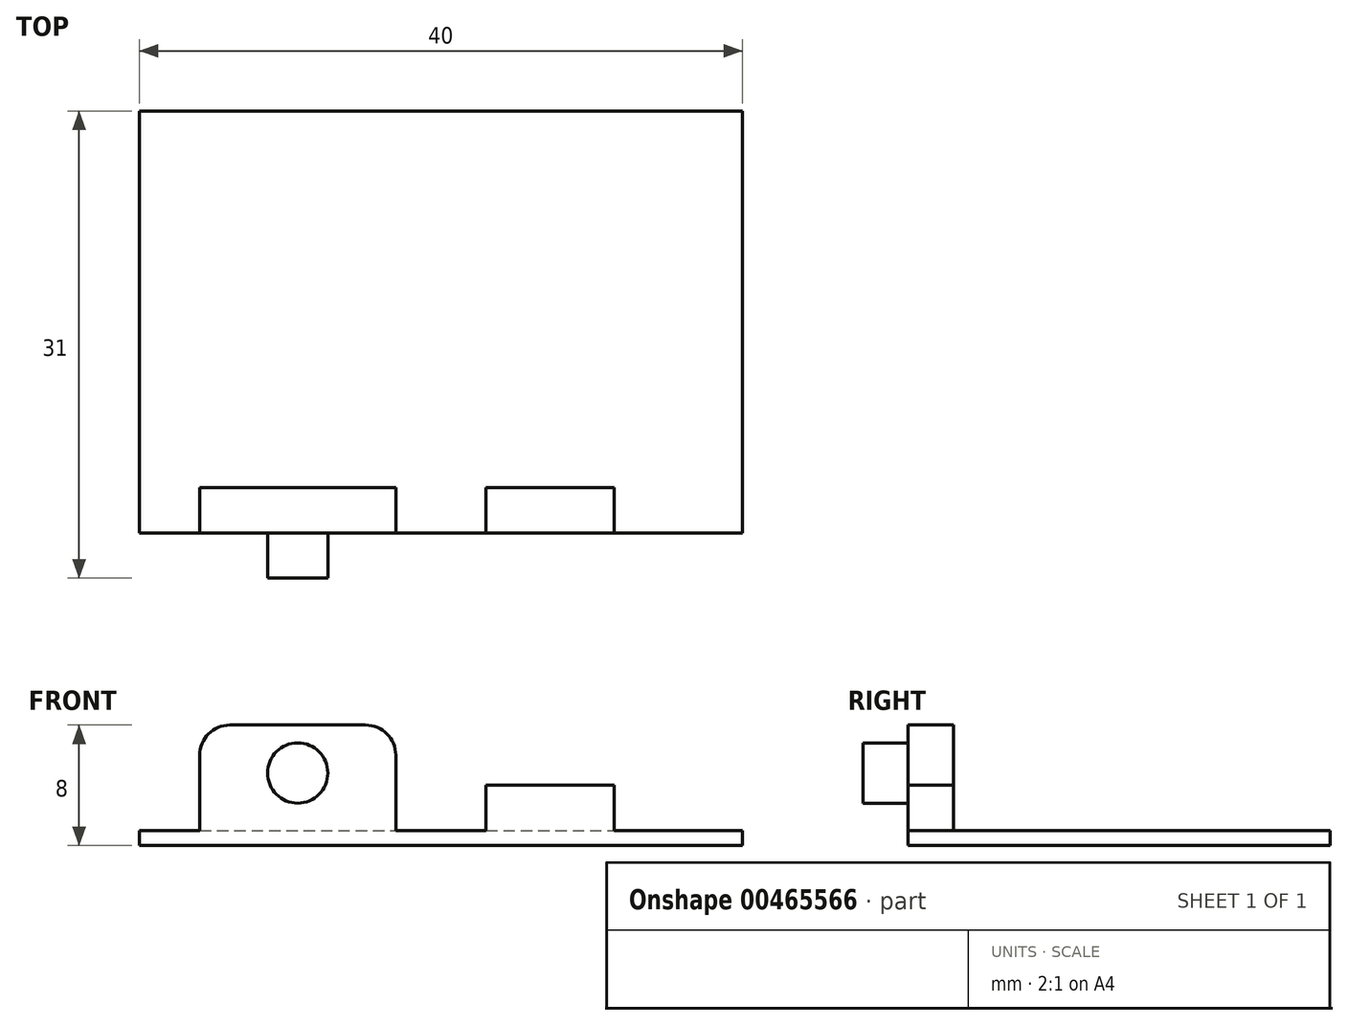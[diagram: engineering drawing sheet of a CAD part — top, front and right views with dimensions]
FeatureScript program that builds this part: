
annotation { "Feature Type Name" : "Feature", "Feature Type Description" : "" }
export const myFeature = defineFeature(function(context is Context, id is Id, definition is map)
    precondition{}
    {
        {
            var Q0;
            Q0=qCreatedBy(makeId("Top.planeOp"),FACE);
            var sketch = newSketch(context, id + "F0", { "sketchPlane" : qUnion([Q0])});
            skLineSegment(sketch, "E0.bottom", {"start": v(20, 14) * mm, "end": v(-20, 14) * mm});
            skLineSegment(sketch, "E0.top", {"start": v(20, -14) * mm, "end": v(-20, -14) * mm});
            skLineSegment(sketch, "E0.left", {"start": v(20, 14) * mm, "end": v(20, -14) * mm});
            skLineSegment(sketch, "E0.right", {"start": v(-20, 14) * mm, "end": v(-20, -14) * mm});
            skPoint(sketch, "E0.middle", {"position": v(0, 0) * mm});
            skSolve(sketch);
        }
        {
            var Q0;
            Q0=makeQuery(id+"F0.imprint","IMPRINT",FACE,{"disambiguationData":[TD([[makeQuery(id+"F0.imprint","IMPRINT",EDGE,{"derivedFrom":sQuery(id+"F0.wireOp",EDGE,"E0.bottom")}),1.0]])]});
            extrude(context, id + "F1", {"entities" : qUnion([Q0]), "depth" : 1 * mm});
        }
        {
            var Q0;
            Q0=makeQuery(id+"F1.opExtrude","CAP_FACE",FACE,{"disambiguationData":[OSD([sQuery(id+"F0.wireOp",EDGE,"E0.bottom"),sQuery(id+"F0.wireOp",EDGE,"E0.top"),sQuery(id+"F0.wireOp",EDGE,"E0.left"),sQuery(id+"F0.wireOp",EDGE,"E0.right")])],"isStart":false});
            var sketch = newSketch(context, id + "F2", { "sketchPlane" : qUnion([Q0])});
            skLineSegment(sketch, "E1.bottom", {"start": v(3, -14) * mm, "end": v(11.5, -14) * mm});
            skLineSegment(sketch, "E1.top", {"start": v(3, -11) * mm, "end": v(11.5, -11) * mm});
            skLineSegment(sketch, "E1.left", {"start": v(3, -14) * mm, "end": v(3, -11) * mm});
            skLineSegment(sketch, "E1.right", {"start": v(11.5, -14) * mm, "end": v(11.5, -11) * mm});
            skLineSegment(sketch, "E2.bottom", {"start": v(-16, -14) * mm, "end": v(-3, -14) * mm});
            skLineSegment(sketch, "E2.top", {"start": v(-16, -11) * mm, "end": v(-3, -11) * mm});
            skLineSegment(sketch, "E2.left", {"start": v(-16, -14) * mm, "end": v(-16, -11) * mm});
            skLineSegment(sketch, "E2.right", {"start": v(-3, -14) * mm, "end": v(-3, -11) * mm});
            skSolve(sketch);
        }
        {
            var Q0;
            Q0=makeQuery(id+"F2.imprint","IMPRINT",FACE,{"disambiguationData":[TD([[makeQuery(id+"F2.imprint","IMPRINT",EDGE,{"derivedFrom":sQuery(id+"F2.wireOp",EDGE,"E2.bottom")}),-1.0]])]});
            extrude(context, id + "F3", {"entities" : qUnion([Q0]), "operationType" : NewBodyOperationType.ADD, "depth" : 7 * mm});
        }
        {
            var Q0;
            Q0=makeQuery(id+"F3.opExtrude","CAP_EDGE",EDGE,{"disambiguationData":[OSD([sQuery(id+"F2.wireOp",EDGE,"E2.left")])],"isStart":false});
            var Q1;
            Q1=makeQuery(id+"F3.opExtrude","CAP_EDGE",EDGE,{"disambiguationData":[OSD([sQuery(id+"F2.wireOp",EDGE,"E2.right")])],"isStart":false});
            fillet(context, id + "F4", {"entities" : qUnion([Q0, Q1]), "radius" : 2 * mm, "tangentPropagation" : true, "allowEdgeOverflow" : false});
        }
        {
            var Q0;
            Q0=makeQuery(id+"F2.imprint","IMPRINT",FACE,{"disambiguationData":[TD([[makeQuery(id+"F2.imprint","IMPRINT",EDGE,{"derivedFrom":sQuery(id+"F2.wireOp",EDGE,"E1.bottom")}),-1.0]])]});
            extrude(context, id + "F5", {"entities" : qUnion([Q0]), "operationType" : NewBodyOperationType.ADD, "depth" : 3 * mm});
        }
        {
            var Q0;
            Q0=makeQuery(id+"F5.boolean.opBoolean","MERGE",FACE,{"derivedFrom":[makeQuery(id+"F3.boolean.opBoolean","MERGE",FACE,{"derivedFrom":[makeQuery(id+"F1.opExtrude","SWEPT_FACE",FACE,{"disambiguationData":[OSD([sQuery(id+"F0.wireOp",EDGE,"E0.top")])]}),makeQuery(id+"F3.opExtrude","SWEPT_FACE",FACE,{"disambiguationData":[OSD([sQuery(id+"F2.wireOp",EDGE,"E2.bottom")])]})]}),makeQuery(id+"F5.opExtrude","SWEPT_FACE",FACE,{"disambiguationData":[OSD([sQuery(id+"F2.wireOp",EDGE,"E1.bottom")])]})]});
            var sketch = newSketch(context, id + "F6", { "sketchPlane" : qUnion([Q0])});
            skCircle(sketch, "E3", {"center": v(-9.5, 4.82) * mm, "radius": 2 * mm});
            skPoint(sketch, "E3.centerSnap0", {"position": v(-9.5, 8) * mm});
            skSolve(sketch);
        }
        {
            var Q0;
            Q0=makeQuery(id+"F6.imprint","IMPRINT",FACE,{"disambiguationData":[TD([[makeQuery(id+"F6.imprint","IMPRINT",EDGE,{"derivedFrom":sQuery(id+"F6.wireOp",EDGE,"E3")}),1.0]])]});
            extrude(context, id + "F7", {"entities" : qUnion([Q0]), "operationType" : NewBodyOperationType.ADD, "depth" : 3 * mm});
        }
    });
